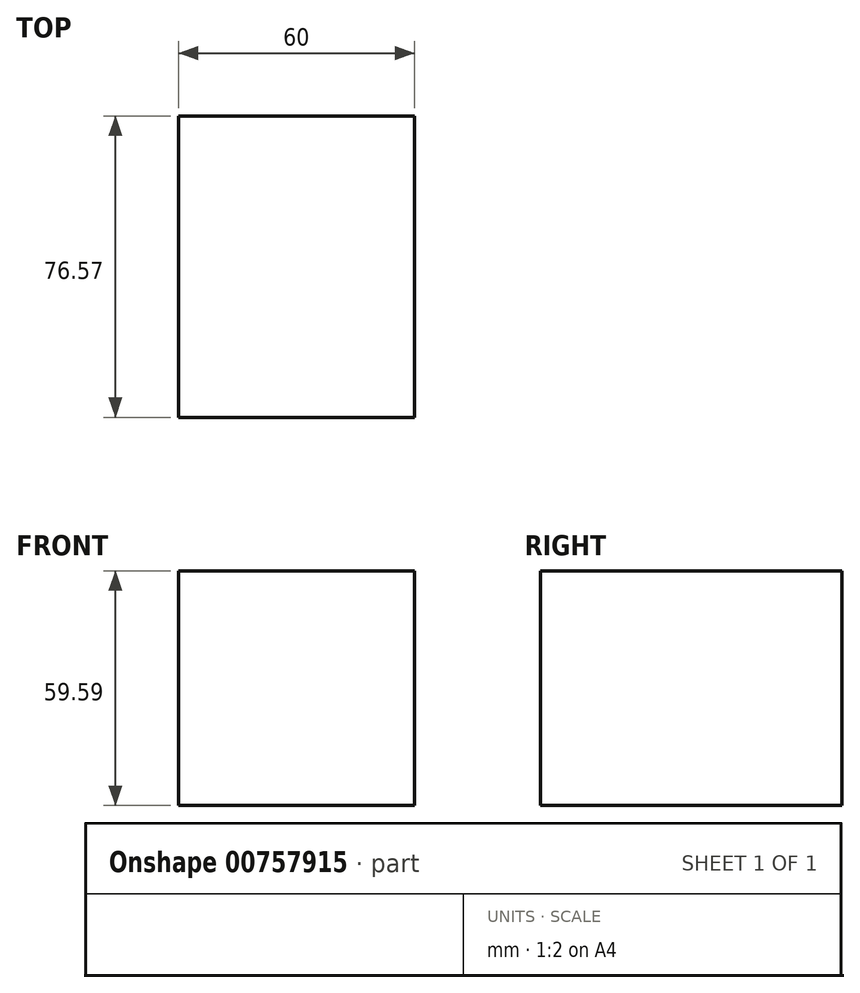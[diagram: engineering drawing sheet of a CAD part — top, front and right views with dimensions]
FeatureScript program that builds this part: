
annotation { "Feature Type Name" : "Feature", "Feature Type Description" : "" }
export const myFeature = defineFeature(function(context is Context, id is Id, definition is map)
    precondition{}
    {
        {
            var Q0;
            Q0=qCreatedBy(makeId("Right.planeOp"),FACE);
            var sketch = newSketch(context, id + "F0", { "sketchPlane" : qUnion([Q0])});
            skLineSegment(sketch, "E0.bottom", {"start": v(-98.45, 59.59) * mm, "end": v(-21.88, 59.59) * mm});
            skLineSegment(sketch, "E0.top", {"start": v(-98.45, 0) * mm, "end": v(-21.88, 0) * mm});
            skLineSegment(sketch, "E0.left", {"start": v(-98.45, 59.59) * mm, "end": v(-98.45, 0) * mm});
            skLineSegment(sketch, "E0.right", {"start": v(-21.88, 59.59) * mm, "end": v(-21.88, 0) * mm});
            skSolve(sketch);
        }
        {
            var Q0;
            Q0 = qSketchRegion(id + "F0", true);
            extrude(context, id + "F1", {"entities" : qUnion([Q0]), "depth" : 60 * mm, "offsetDistance" : 25 * mm});
        }
    });
